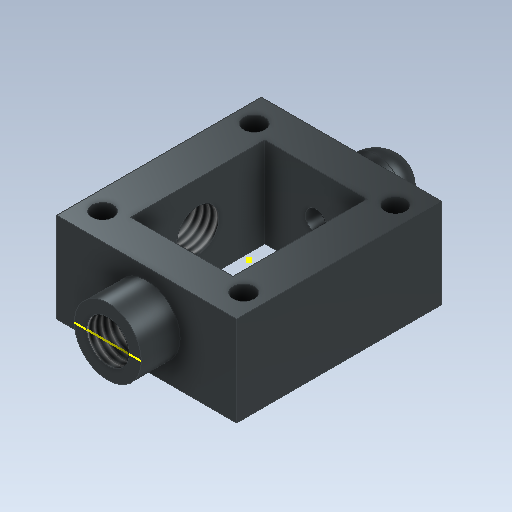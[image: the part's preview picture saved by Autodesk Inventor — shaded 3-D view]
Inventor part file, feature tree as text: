
AUTODESK INVENTOR PART (.ipt)
format: ipt  version: 2020 (Build 240168000, 168)  size: 210,944 bytes
history: native  units: mm
features: sketch x10, extrude x5, hole x4, thread x2, fillet x2, projected_geometry x1
ambient origin geometry x8: Origin, YZ Plane, XZ Plane, XY Plane, X Axis, Y Axis, Z Axis, Center Point
bodies: Solid1 (feature_tree)
feature tree (24):
  extrude  "Extrusion1"  Depth=29.0mm
  extrude  "Extrusion2"  Depth=14.5mm
  sketch  "Sketch3"  dims[d5=19.0mm d6=12.75mm d7=0.0mm]
  extrude  "Extrusion3"  Depth=12.75mm TaperAngle=0.0deg
  extrude  "Extrusion6"  Depth=3.0mm
  extrude  "Extrusion7"  Depth=20.0mm
  hole  "Hole1"  [1 undecoded]
  thread  "Thread2"  [1 undecoded]
  fillet  "Fillet1"  Radius=8.0mm
  hole  "Hole2"  [1 undecoded]
  hole  "Hole3"  [1 undecoded]
  thread  "Thread3"  [1 undecoded]
  fillet  "Fillet2"  Radius=6.0mm
  sketch  "Sketch12"  dims[d50=6.0mm d51=6.0mm d52=4.0mm d53=2.0mm d54=90.0deg d55=6.0mm d56=20.594885mm]
  sketch  "Sketch13"  dims[d57=3.0mm d58=6.0mm d59=4.0mm d60=2.0mm d61=90.0deg d62=6.0mm d63=20.594885mm d64=6.0mm d65=0.0mm d66=4.0mm d67=38.0mm d68=3.0mm d69=6.0mm d70=4.0mm d71=2.0mm d72=90.0deg d73=8.5mm d74=20.594885mm]
  hole  "Hole4"  [1 undecoded]
  sketch  "Sketch1"  dims[d0=25.5mm d1=29.0mm]
  sketch  "Sketch2"  dims[d2=12.75mm d3=0.0mm d4=14.5mm]
  sketch  "Sketch4"  dims[d8=3.0mm d9=3.75mm]
  sketch  "Sketch7"  dims[d10=2.75mm d11=20.0mm d13=20.0mm d14=20.0mm d16=21.5mm]
  sketch  "Sketch8"  dims[d19=9.5mm d20=5.5mm d21=0.0mm d30=0.0mm d31=0.0mm d32=8.0mm]
  sketch  "Sketch10"  dims[d33=7.5mm d34=0.0mm d35=6.0mm]
  sketch  "Sketch11"  dims[d36=6.0mm d37=6.0mm d38=4.0mm d39=2.0mm d40=90.0deg d41=8.0mm d42=20.594885mm d43=5.5mm d44=0.0mm d45=4.75mm]
  projected_geometry  "Projected Loop1"
note: 6 required parameter values undecoded (feature->parameter linkage not recoverable at this tier; creation-order binding heuristic only, values carry confidence <= 0.55)
